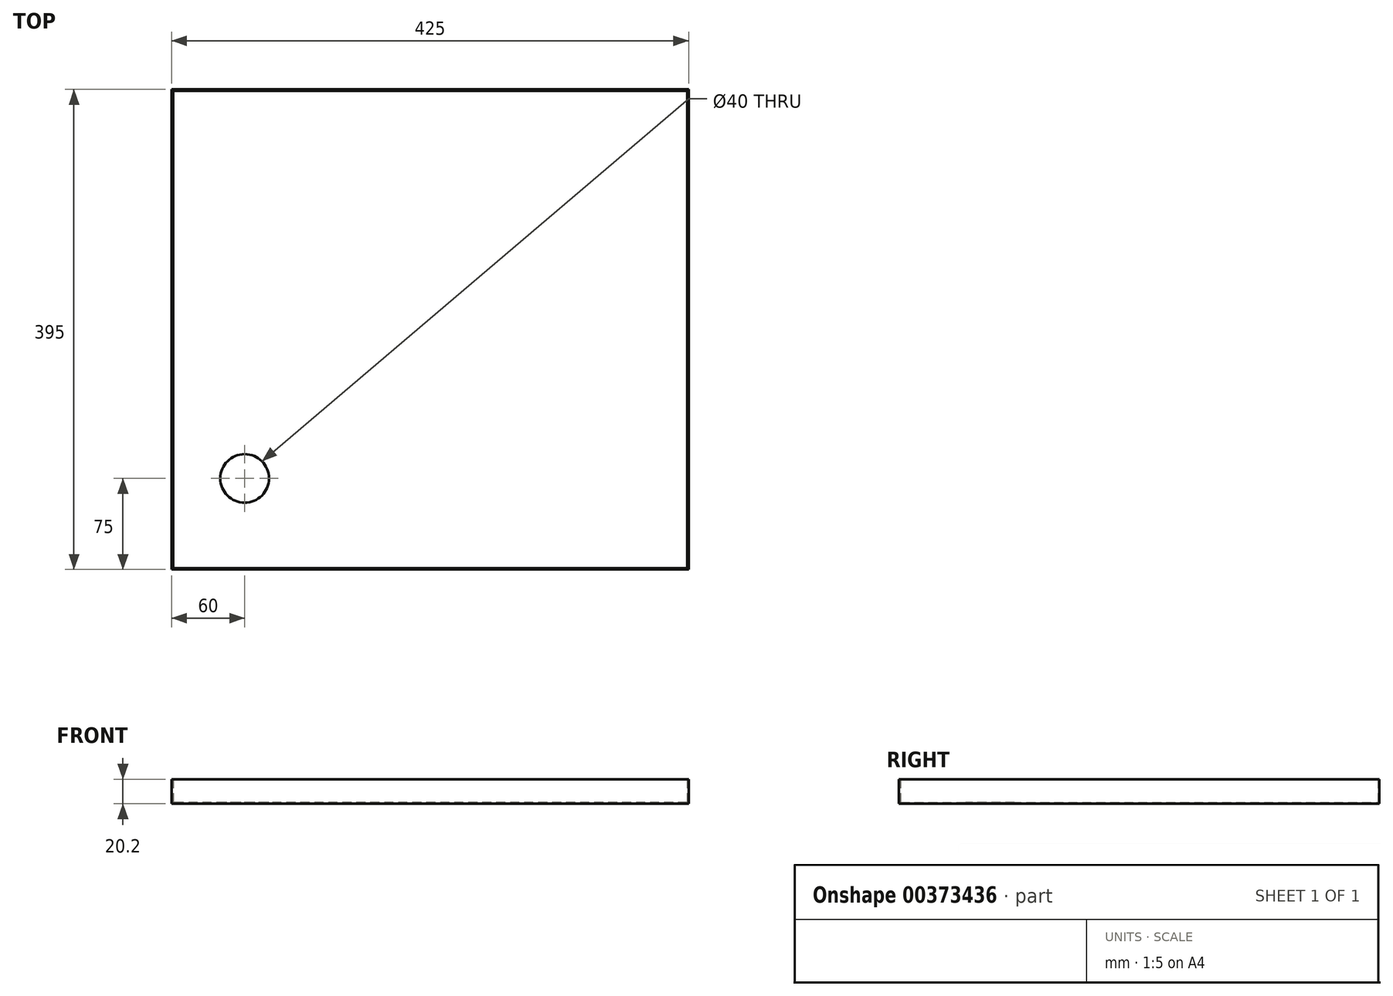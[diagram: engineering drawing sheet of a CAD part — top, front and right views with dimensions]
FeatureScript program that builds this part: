
annotation { "Feature Type Name" : "Feature", "Feature Type Description" : "" }
export const myFeature = defineFeature(function(context is Context, id is Id, definition is map)
    precondition{}
    {
        {
            var Q0;
            Q0=qCreatedBy(makeId("Top.planeOp"),FACE);
            var sketch = newSketch(context, id + "F0", { "sketchPlane" : qUnion([Q0])});
            skLineSegment(sketch, "E0.bottom", {"start": v(212.5, -197.5) * mm, "end": v(-212.5, -197.5) * mm});
            skLineSegment(sketch, "E0.top", {"start": v(212.5, 197.5) * mm, "end": v(-212.5, 197.5) * mm});
            skLineSegment(sketch, "E0.left", {"start": v(212.5, -197.5) * mm, "end": v(212.5, 197.5) * mm});
            skLineSegment(sketch, "E0.right", {"start": v(-212.5, -197.5) * mm, "end": v(-212.5, 197.5) * mm});
            skPoint(sketch, "E0.middle", {"position": v(0, 0) * mm});
            skLineSegment(sketch, "E1", {"start": v(-152.5, -197.5) * mm, "end": v(-152.5, -122.5) * mm, "construction": true});
            skCircle(sketch, "E2", {"center": v(-152.5, -122.5) * mm, "radius": 20 * mm});
            skSolve(sketch);
        }
        {
            var Q0;
            Q0 = qSketchRegion(id + "F0", true);
            extrude(context, id + "F1", {"entities" : qUnion([Q0]), "depth" : 1.2 * mm});
        }
        {
            var Q0;
            Q0=makeQuery(id+"F1.opExtrude","CAP_FACE",FACE,{"disambiguationData":[OSD([sQuery(id+"F0.wireOp",EDGE,"E0.bottom"),sQuery(id+"F0.wireOp",EDGE,"E0.top"),sQuery(id+"F0.wireOp",EDGE,"E0.left"),sQuery(id+"F0.wireOp",EDGE,"E0.right"),sQuery(id+"F0.wireOp",EDGE,"E2")])],"isStart":false});
            var sketch = newSketch(context, id + "F2", { "sketchPlane" : qUnion([Q0])});
            skLineSegment(sketch, "E3.bottom", {"start": v(211.3, -196.3) * mm, "end": v(-211.3, -196.3) * mm});
            skLineSegment(sketch, "E3.top", {"start": v(211.3, 196.3) * mm, "end": v(-211.3, 196.3) * mm});
            skLineSegment(sketch, "E3.left", {"start": v(211.3, -196.3) * mm, "end": v(211.3, 196.3) * mm});
            skLineSegment(sketch, "E3.right", {"start": v(-211.3, -196.3) * mm, "end": v(-211.3, 196.3) * mm});
            skPoint(sketch, "E3.middle", {"position": v(0, 0) * mm});
            skSolve(sketch);
        }
        {
            var Q0;
            Q0=makeQuery(id+"F2.imprint","IMPRINT",FACE,{"disambiguationData":[TD([[makeQuery(id+"F2.imprint","IMPRINT",EDGE,{"derivedFrom":sQuery(id+"F2.wireOp",EDGE,"E3.bottom")}),1.0]])]});
            extrude(context, id + "F3", {"entities" : qUnion([Q0]), "operationType" : NewBodyOperationType.ADD, "depth" : 19 * mm});
        }
    });
